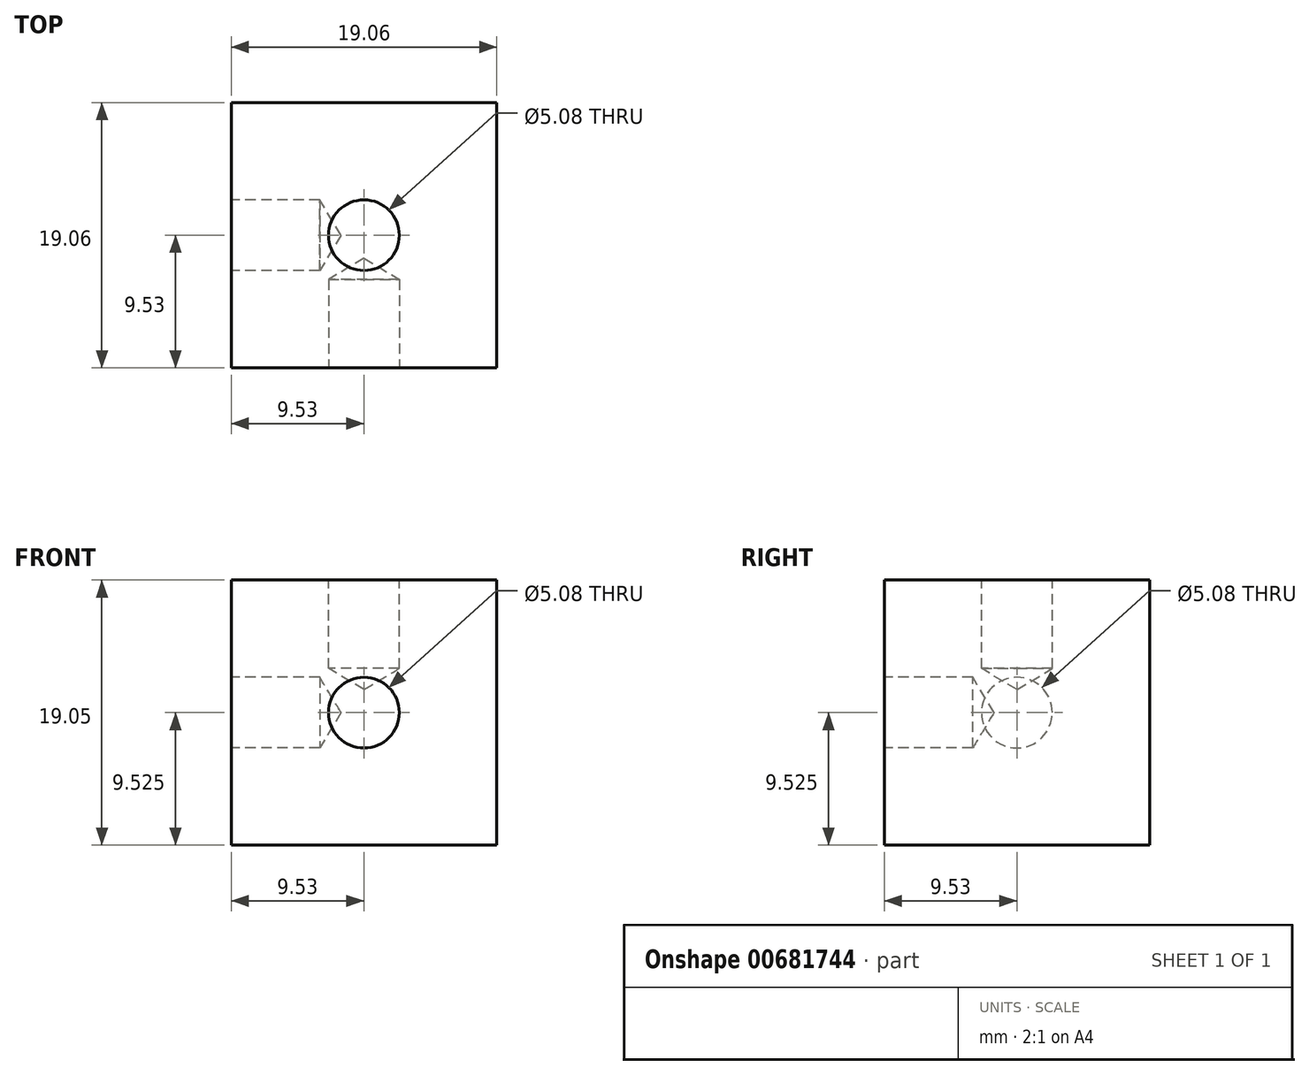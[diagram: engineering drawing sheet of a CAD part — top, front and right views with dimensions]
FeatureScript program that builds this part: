
annotation { "Feature Type Name" : "Feature", "Feature Type Description" : "" }
export const myFeature = defineFeature(function(context is Context, id is Id, definition is map)
    precondition{}
    {
        {
            var Q0;
            Q0=qCreatedBy(makeId("Top.planeOp"),FACE);
            var sketch = newSketch(context, id + "F0", { "sketchPlane" : qUnion([Q0])});
            skLineSegment(sketch, "E0.bottom", {"start": v(-9.53, -9.53) * mm, "end": v(9.53, -9.53) * mm});
            skLineSegment(sketch, "E0.top", {"start": v(-9.53, 9.53) * mm, "end": v(9.52, 9.53) * mm});
            skLineSegment(sketch, "E0.left", {"start": v(-9.53, -9.53) * mm, "end": v(-9.53, 9.53) * mm});
            skLineSegment(sketch, "E0.right", {"start": v(9.53, -9.53) * mm, "end": v(9.52, 9.53) * mm});
            skPoint(sketch, "E0.middle", {"position": v(0, 0) * mm});
            skSolve(sketch);
        }
        {
            var Q0;
            Q0=makeQuery(id+"F0.imprint","IMPRINT",FACE,{"disambiguationData":[TD([[makeQuery(id+"F0.imprint","IMPRINT",EDGE,{"derivedFrom":sQuery(id+"F0.wireOp",EDGE,"E0.bottom")}),1.0]])]});
            extrude(context, id + "F1", {"entities" : qUnion([Q0]), "depth" : 19.05 * mm, "offsetDistance" : 25.4 * mm});
        }
        {
            var Q0;
            Q0=makeQuery(id+"F1.opExtrude","SWEPT_FACE",FACE,{"disambiguationData":[OSD([sQuery(id+"F0.wireOp",EDGE,"E0.bottom")])]});
            var sketch = newSketch(context, id + "F2", { "sketchPlane" : qUnion([Q0])});
            skCircle(sketch, "E1", {"center": v(0, 9.53) * mm, "radius": 2.54 * mm});
            skSolve(sketch);
        }
        {
            var Q0;
            Q0=sQuery(id+"F2.wireOp",VERTEX,"E1.center");
            var Q1;
            Q1=makeQuery(id+"F1.opExtrude","SWEPT_BODY",BODY,{"disambiguationData":[OSD([sQuery(id+"F0.wireOp",EDGE,"E0.bottom"),sQuery(id+"F0.wireOp",EDGE,"E0.top"),sQuery(id+"F0.wireOp",EDGE,"E0.left"),sQuery(id+"F0.wireOp",EDGE,"E0.right")])]});
            hole(context, id + "F3", {"style" : HoleStyle.SIMPLE, "endStyle" : HoleEndStyle.BLIND, "holeDiameter" : 5.08 * mm, "majorDiameter" : 6.35 * mm, "holeDepth" : 6.35 * mm, "isTappedThrough" : true, "tappedDepth" : 12.7 * mm, "tapClearance" : 3, "startFromSketch" : true, "locations" : qUnion([Q0]), "scope" : qUnion([Q1])});
        }
        {
            var Q0;
            Q0=makeQuery(id+"F1.opExtrude","SWEPT_FACE",FACE,{"disambiguationData":[OSD([sQuery(id+"F0.wireOp",EDGE,"E0.left")])]});
            var sketch = newSketch(context, id + "F4", { "sketchPlane" : qUnion([Q0])});
            skCircle(sketch, "E2", {"center": v(0, 9.53) * mm, "radius": 2.54 * mm});
            skSolve(sketch);
        }
        {
            var Q0;
            Q0=sQuery(id+"F4.wireOp",VERTEX,"E2.center");
            var Q1;
            Q1=makeQuery(id+"F1.opExtrude","SWEPT_BODY",BODY,{"disambiguationData":[OSD([sQuery(id+"F0.wireOp",EDGE,"E0.bottom"),sQuery(id+"F0.wireOp",EDGE,"E0.top"),sQuery(id+"F0.wireOp",EDGE,"E0.left"),sQuery(id+"F0.wireOp",EDGE,"E0.right")])]});
            hole(context, id + "F5", {"style" : HoleStyle.SIMPLE, "endStyle" : HoleEndStyle.BLIND, "holeDiameter" : 5.08 * mm, "majorDiameter" : 6.35 * mm, "holeDepth" : 6.35 * mm, "isTappedThrough" : true, "tappedDepth" : 12.7 * mm, "tapClearance" : 3, "startFromSketch" : true, "locations" : qUnion([Q0]), "scope" : qUnion([Q1])});
        }
        {
            var Q0;
            Q0=makeQuery(id+"F1.opExtrude","CAP_FACE",FACE,{"disambiguationData":[OSD([sQuery(id+"F0.wireOp",EDGE,"E0.bottom"),sQuery(id+"F0.wireOp",EDGE,"E0.top"),sQuery(id+"F0.wireOp",EDGE,"E0.left"),sQuery(id+"F0.wireOp",EDGE,"E0.right")])],"isStart":false});
            var sketch = newSketch(context, id + "F6", { "sketchPlane" : qUnion([Q0])});
            skCircle(sketch, "E3", {"center": v(0, 0) * mm, "radius": 2.54 * mm});
            skSolve(sketch);
        }
        {
            var Q0;
            Q0=sQuery(id+"F6.wireOp",VERTEX,"E3.center");
            var Q1;
            Q1=makeQuery(id+"F1.opExtrude","SWEPT_BODY",BODY,{"disambiguationData":[OSD([sQuery(id+"F0.wireOp",EDGE,"E0.bottom"),sQuery(id+"F0.wireOp",EDGE,"E0.top"),sQuery(id+"F0.wireOp",EDGE,"E0.left"),sQuery(id+"F0.wireOp",EDGE,"E0.right")])]});
            hole(context, id + "F7", {"style" : HoleStyle.SIMPLE, "endStyle" : HoleEndStyle.BLIND, "holeDiameter" : 5.08 * mm, "majorDiameter" : 6.35 * mm, "holeDepth" : 6.35 * mm, "isTappedThrough" : true, "tappedDepth" : 12.7 * mm, "tapClearance" : 3, "startFromSketch" : true, "locations" : qUnion([Q0]), "scope" : qUnion([Q1])});
        }
    });
